# Revit family: AIPhone_GTA-DES
name_source: partatom
category: Data Devices
units: mm (PartAtom-declared; Revit-internal decimal feet)

## family parameters
Classification Number = 23.85.50.17
Cut with Voids When Loaded = No
Host = Face
Maintain Annotation Orientation = Yes
Part Type = Normal
Room Calculation Point = No
Round Connector Dimension = Use Diameter
Shared = No

## types (1)
- AIPhone_GTA-DES
    Body Color = Body Color
    Buttons = Silver Trim
    Default Elevation = 48 "
    Depth = 0.56 "
    Description = AUDIO ENTRANCE PANEL
    Door Release Button = Door Release
    Green Building-LEED = https://www.arcat.com
    Height = 12.63 "
    Host Width = 24 "
    Installation-Fabrication = https://www.arcat.com
    Manufacturer = AIPHONE
    Manufacturer Fax = 425-455-0071
    Manufacturer Website = www.aiphone.com
    Model = GTA-DES
    Revision = R1.0.0
    Screen = Screen
    Specification = https://www.arcat.com
    Talk Button = Talk Button
    Width = 5.31 "

## geometry (parser evidence)
native form markers: Sweep x2
no freeform markers — native parametric forms only
